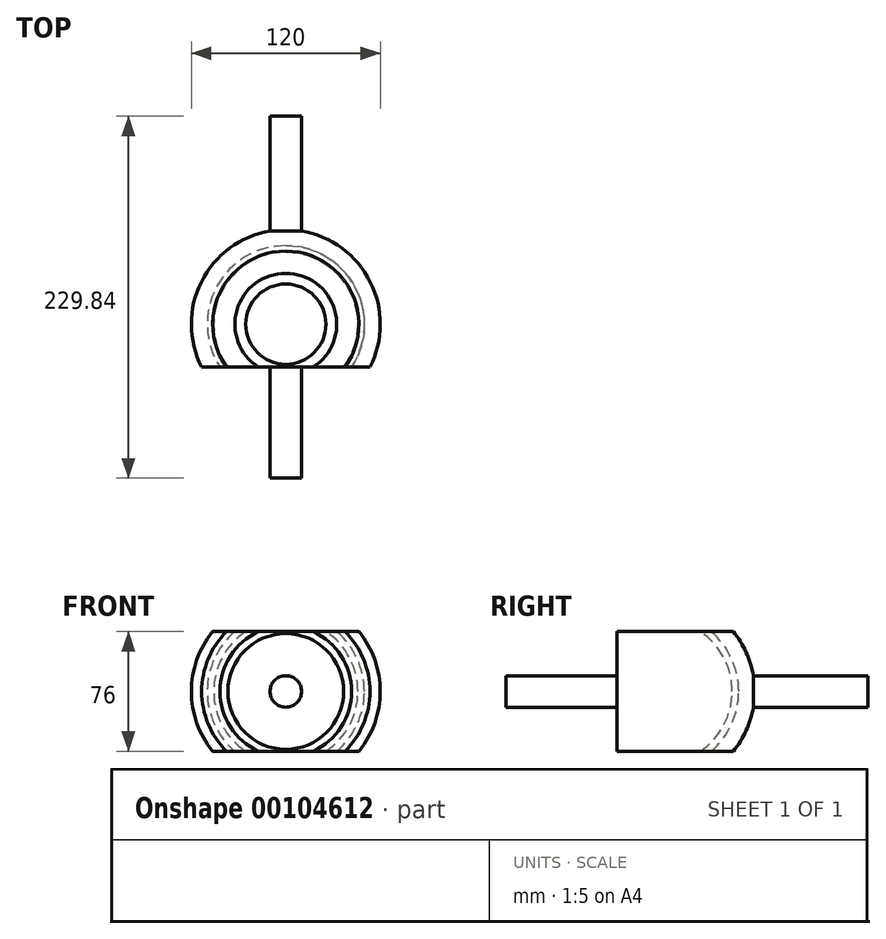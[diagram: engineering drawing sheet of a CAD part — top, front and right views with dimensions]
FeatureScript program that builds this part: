
annotation { "Feature Type Name" : "Feature", "Feature Type Description" : "" }
export const myFeature = defineFeature(function(context is Context, id is Id, definition is map)
    precondition{}
    {
        {
            var Q0;
            Q0=qCreatedBy(makeId("Top.planeOp"),FACE);
            var sketch = newSketch(context, id + "F0", { "sketchPlane" : qUnion([Q0])});
            skArc(sketch, "E0", {"start": v(0, 60) * mm, "mid": v(-51.17, 31.33) * mm, "end": v(-53.44, -27.29) * mm});
            skLineSegment(sketch, "E1", {"start": v(-60, 0) * mm, "end": v(-49.9, 0) * mm});
            skArc(sketch, "E2", {"start": v(0, 49.9) * mm, "mid": v(-43.87, 23.78) * mm, "end": v(-41.81, -27.23) * mm});
            skLineSegment(sketch, "E3", {"start": v(-53.44, -27.29) * mm, "end": v(-41.81, -27.23) * mm});
            skPoint(sketch, "E4", {"position": v(-49.9, 0) * mm});
            skArc(sketch, "E5", {"start": v(0, 45.76) * mm, "mid": v(-40.88, 20.56) * mm, "end": v(-36.73, -27.29) * mm});
            skLineSegment(sketch, "E6", {"start": v(-36.73, -27.29) * mm, "end": v(0, -27.29) * mm});
            skLineSegment(sketch, "E7.bottom", {"start": v(-10, -27.29) * mm, "end": v(0, -27.29) * mm});
            skLineSegment(sketch, "E7.top", {"start": v(-10, -97.76) * mm, "end": v(0, -97.76) * mm});
            skLineSegment(sketch, "E7.left", {"start": v(-10, -27.29) * mm, "end": v(-10, -97.76) * mm});
            skLineSegment(sketch, "E8", {"start": v(-10, 132.08) * mm, "end": v(0, 132.08) * mm});
            skLineSegment(sketch, "E9", {"start": v(-10, 132.08) * mm, "end": v(-10, 59.16) * mm});
            skLineSegment(sketch, "E10.left", {"start": v(0, -97.76) * mm, "end": v(0, 144.54) * mm});
            skSolve(sketch);
        }
        {
            var Q0;
            Q0=qCreatedBy(makeId("Top.planeOp"),FACE);
            var sketch = newSketch(context, id + "F1", { "sketchPlane" : qUnion([Q0])});
            skLineSegment(sketch, "E11", {"start": v(0, -59.96) * mm, "end": v(0, 150.13) * mm});
            skSolve(sketch);
        }
        {
            var Q0;
            Q0 = qSketchRegion(id + "F0", true);
            var Q1;
            Q1=sQuery(id+"F1.wireOp",EDGE,"E11");
            revolve(context, id + "F2", {"entities" : qUnion([Q0]), "axis" : qUnion([Q1]), "revolveType" : RevolveType.FULL});
        }
        {
            var Q0;
            Q0=qCreatedBy(makeId("Top.planeOp"),FACE);
            cPlane(context, id + "F3", {"entities" : qUnion([Q0]), "cplaneType" : CPlaneType.OFFSET, "offset" : 38 * mm, "width" : 150 * mm, "height" : 150 * mm});
        }
        {
            var Q0;
            Q0=qCreatedBy(id+"F3.planeOp",FACE);
            var sketch = newSketch(context, id + "F4", { "sketchPlane" : qUnion([Q0])});
            skLineSegment(sketch, "E12.bottom", {"start": v(67.91, 64.68) * mm, "end": v(-73.18, 64.68) * mm});
            skLineSegment(sketch, "E12.top", {"start": v(67.91, -61.93) * mm, "end": v(-73.18, -61.93) * mm});
            skLineSegment(sketch, "E12.left", {"start": v(67.91, 64.68) * mm, "end": v(67.91, -61.93) * mm});
            skLineSegment(sketch, "E12.right", {"start": v(-73.18, 64.68) * mm, "end": v(-73.18, -61.93) * mm});
            skSolve(sketch);
        }
        {
            var Q0;
            Q0 = qSketchRegion(id + "F4", true);
            extrude(context, id + "F5", {"entities" : qUnion([Q0]), "depth" : 30 * mm});
        }
        {
            var Q0;
            Q0=makeQuery(id+"F5.opExtrude","SWEPT_BODY",BODY,{"disambiguationData":[OSD([sQuery(id+"F4.wireOp",EDGE,"E12.bottom"),sQuery(id+"F4.wireOp",EDGE,"E12.top"),sQuery(id+"F4.wireOp",EDGE,"E12.left"),sQuery(id+"F4.wireOp",EDGE,"E12.right")])]});
            var Q1;
            Q1=qCreatedBy(makeId("Top.planeOp"),FACE);
            mirror(context, id + "F6", {"entities" : qUnion([Q0]), "mirrorPlane" : qUnion([Q1])});
        }
        {
            var Q0;
            Q0=makeQuery(id+"F5.opExtrude","SWEPT_BODY",BODY,{"disambiguationData":[OSD([sQuery(id+"F4.wireOp",EDGE,"E12.bottom"),sQuery(id+"F4.wireOp",EDGE,"E12.top"),sQuery(id+"F4.wireOp",EDGE,"E12.left"),sQuery(id+"F4.wireOp",EDGE,"E12.right")])]});
            var Q1;
            Q1=makeQuery(id+"F6.opPattern","COPY",BODY,{"derivedFrom":makeQuery(id+"F5.opExtrude","SWEPT_BODY",BODY,{"disambiguationData":[OSD([sQuery(id+"F4.wireOp",EDGE,"E12.bottom"),sQuery(id+"F4.wireOp",EDGE,"E12.top"),sQuery(id+"F4.wireOp",EDGE,"E12.left"),sQuery(id+"F4.wireOp",EDGE,"E12.right")])]}),"instanceName":"1"});
            var Q2;
            Q2=makeQuery(id+"F2.opRevolve","SWEPT_BODY",BODY,{"disambiguationData":[OSD([sQuery(id+"F0.wireOp",EDGE,"E0"),sQuery(id+"F0.wireOp",EDGE,"E2"),sQuery(id+"F0.wireOp",EDGE,"E3"),sQuery(id+"F0.wireOp",EDGE,"E8"),sQuery(id+"F0.wireOp",EDGE,"E9"),sQuery(id+"F0.wireOp",EDGE,"E10.left")])]});
            var Q3;
            Q3=makeQuery(id+"F2.opRevolve","SWEPT_BODY",BODY,{"disambiguationData":[OSD([sQuery(id+"F0.wireOp",EDGE,"E5"),sQuery(id+"F0.wireOp",EDGE,"E6"),sQuery(id+"F0.wireOp",EDGE,"E7.top"),sQuery(id+"F0.wireOp",EDGE,"E7.left"),sQuery(id+"F0.wireOp",EDGE,"E10.left")])]});
            booleanBodies(context, id + "F7", {"operationType" : BooleanOperationType.SUBTRACTION, "tools" : qUnion([Q0, Q1]), "targets" : qUnion([Q2, Q3])});
        }
    });
